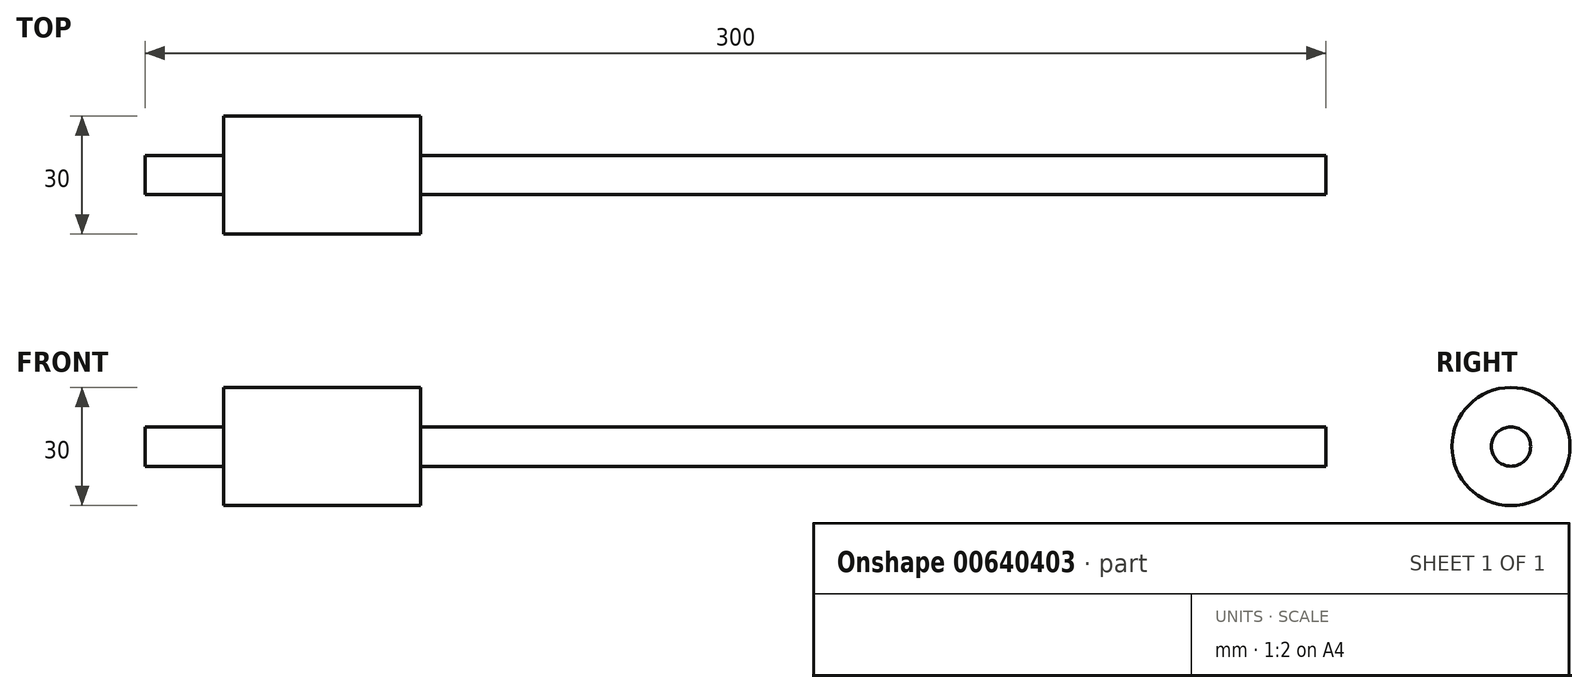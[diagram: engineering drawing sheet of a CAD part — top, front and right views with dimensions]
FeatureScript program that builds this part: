
annotation { "Feature Type Name" : "Feature", "Feature Type Description" : "" }
export const myFeature = defineFeature(function(context is Context, id is Id, definition is map)
    precondition{}
    {
        {
            var Q0;
            Q0=qCreatedBy(makeId("Top.planeOp"),FACE);
            var sketch = newSketch(context, id + "F0", { "sketchPlane" : qUnion([Q0])});
            skLineSegment(sketch, "E0.bottom", {"start": v(-50, 15) * mm, "end": v(0, 15) * mm});
            skLineSegment(sketch, "E0.top", {"start": v(-50, 0) * mm, "end": v(0, 0) * mm});
            skLineSegment(sketch, "E0.left", {"start": v(-50, 15) * mm, "end": v(-50, 0) * mm});
            skLineSegment(sketch, "E0.right", {"start": v(0, 15) * mm, "end": v(0, 0) * mm});
            skLineSegment(sketch, "E1.bottom", {"start": v(-70, 5) * mm, "end": v(230, 5) * mm});
            skLineSegment(sketch, "E1.top", {"start": v(-70, 0) * mm, "end": v(230, 0) * mm});
            skLineSegment(sketch, "E1.left", {"start": v(-70, 5) * mm, "end": v(-70, 0) * mm});
            skLineSegment(sketch, "E1.right", {"start": v(230, 5) * mm, "end": v(230, 0) * mm});
            skSolve(sketch);
        }
        {
            var Q0;
            {var subQ5=sQuery(id+"F0.wireOp",EDGE,"E1.left");Q0=makeQuery(id+"F0.imprint","IMPRINT",FACE,{"disambiguationData":[TD([[makeQuery(id+"F0.imprint","IMPRINT",EDGE,{"derivedFrom":subQ5}),1.0]])]});}
            var Q1;
            {var subQ0=sQuery(id+"F0.wireOp",EDGE,"E0.bottom");Q1=makeQuery(id+"F0.imprint","IMPRINT",FACE,{"disambiguationData":[TD([[makeQuery(id+"F0.imprint","IMPRINT",EDGE,{"derivedFrom":subQ0}),-1.0]])]});}
            var Q2;
            {var subQ0=sQuery(id+"F0.wireOp",EDGE,"E1.top");var subQ1=sQuery(id+"F0.wireOp",EDGE,"E0.left");var subQ2=makeQuery(id+"F0.imprint","INTERSECT",VERTEX,{"derivedFrom":[subQ1,subQ0]});Q2=makeQuery(id+"F0.imprint","IMPRINT",FACE,{"disambiguationData":[TD([[makeQuery(id+"F0.imprint","IMPRINT",EDGE,{"disambiguationData":[TD([[subQ2,1.0]])],"derivedFrom":subQ1}),1.0]])]});}
            var Q3;
            {var subQ5=sQuery(id+"F0.wireOp",EDGE,"E1.right");Q3=makeQuery(id+"F0.imprint","IMPRINT",FACE,{"disambiguationData":[TD([[makeQuery(id+"F0.imprint","IMPRINT",EDGE,{"derivedFrom":subQ5}),-1.0]])]});}
            var Q4;
            Q4=sQuery(id+"F0.wireOp",EDGE,"E1.top");
            revolve(context, id + "F1", {"entities" : qUnion([Q0, Q1, Q2, Q3]), "axis" : qUnion([Q4]), "revolveType" : RevolveType.FULL});
        }
    });
